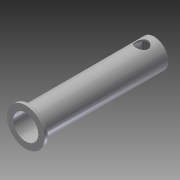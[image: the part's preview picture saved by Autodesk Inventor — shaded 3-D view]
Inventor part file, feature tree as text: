
AUTODESK INVENTOR PART (.ipt)
format: ipt  version: 2013 (Build 170138000, 138)  size: 108,032 bytes
history: native  units: in
note: dims shown in document units (in); Inventor stores cm internally (conversion verified against a paired STEP export)
features: extrude x3, sketch x3, plane x2
ambient origin geometry x8: Origin, YZ Plane, XZ Plane, XY Plane, X Axis, Y Axis, Z Axis, Center Point
bodies: Solid1 (feature_tree)
feature tree (8):
  extrude  "Extrusion1"  Depth=0.4in
  extrude  "Extrusion2"  Depth=0.6in
  plane  "Work Plane2"
  extrude  "Extrusion3"  Depth=0.25in TaperAngle=90.0deg
  sketch  "Sketch1"  dims[d0=0.45in d1=0.4in]
  sketch  "Sketch2"  dims[d2=2.0in d3=0.0in d4=0.6in]
  plane  "Work Plane1"
  sketch  "Sketch3"  dims[d5=0.05in d6=0.0in d7=90.0deg d8=0.25in d9=0.2in d10=0.2in d11=1.0in d12=0.0in]
